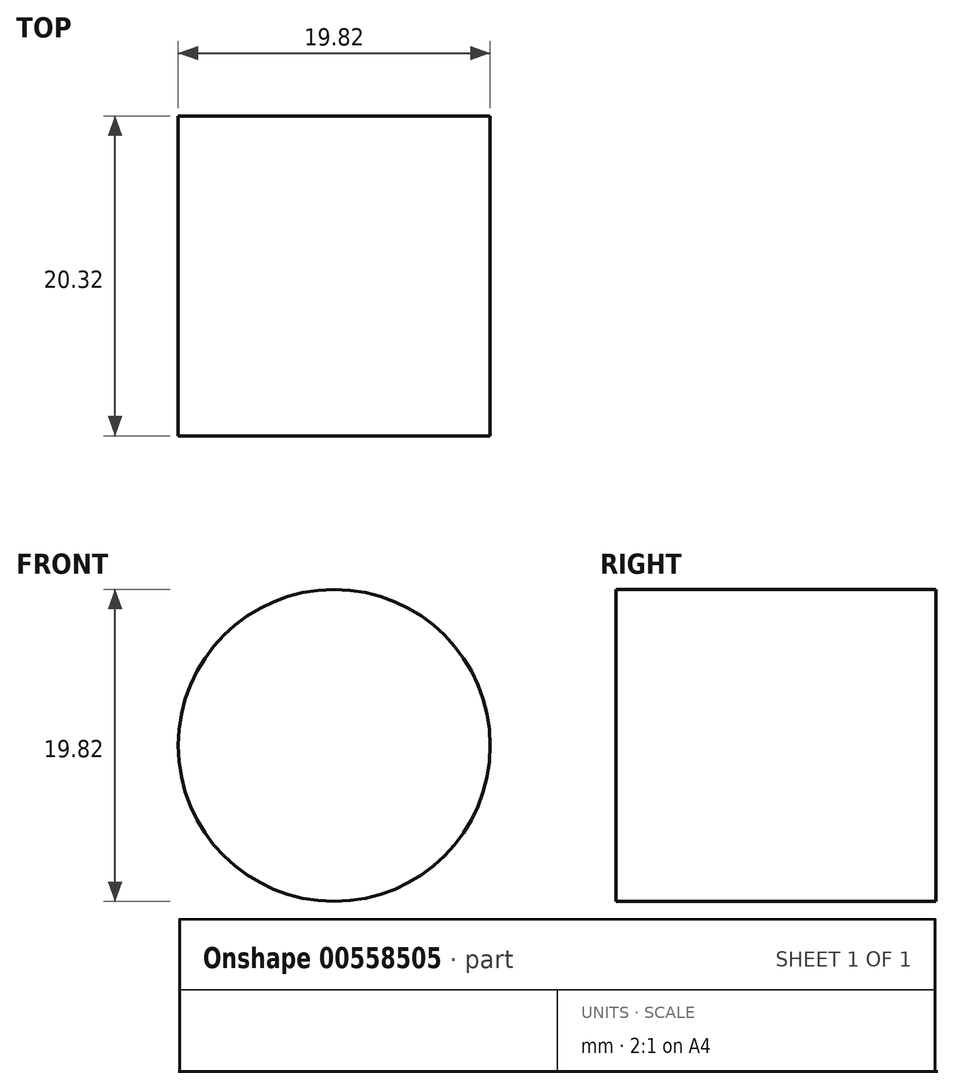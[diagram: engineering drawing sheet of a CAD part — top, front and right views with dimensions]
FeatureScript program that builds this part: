
annotation { "Feature Type Name" : "Feature", "Feature Type Description" : "" }
export const myFeature = defineFeature(function(context is Context, id is Id, definition is map)
    precondition{}
    {
        {
            var Q0;
            Q0=qCreatedBy(makeId("Front.planeOp"),FACE);
            var sketch = newSketch(context, id + "F0", { "sketchPlane" : qUnion([Q0])});
            skCircle(sketch, "E0", {"center": v(0, 0) * mm, "radius": 9.9 * mm});
            skSolve(sketch);
        }
        {
            var Q0;
            Q0 = qSketchRegion(id + "F0", true);
            extrude(context, id + "F1", {"entities" : qUnion([Q0]), "depth" : 20.32 * mm, "offsetDistance" : 25.4 * mm});
        }
    });
